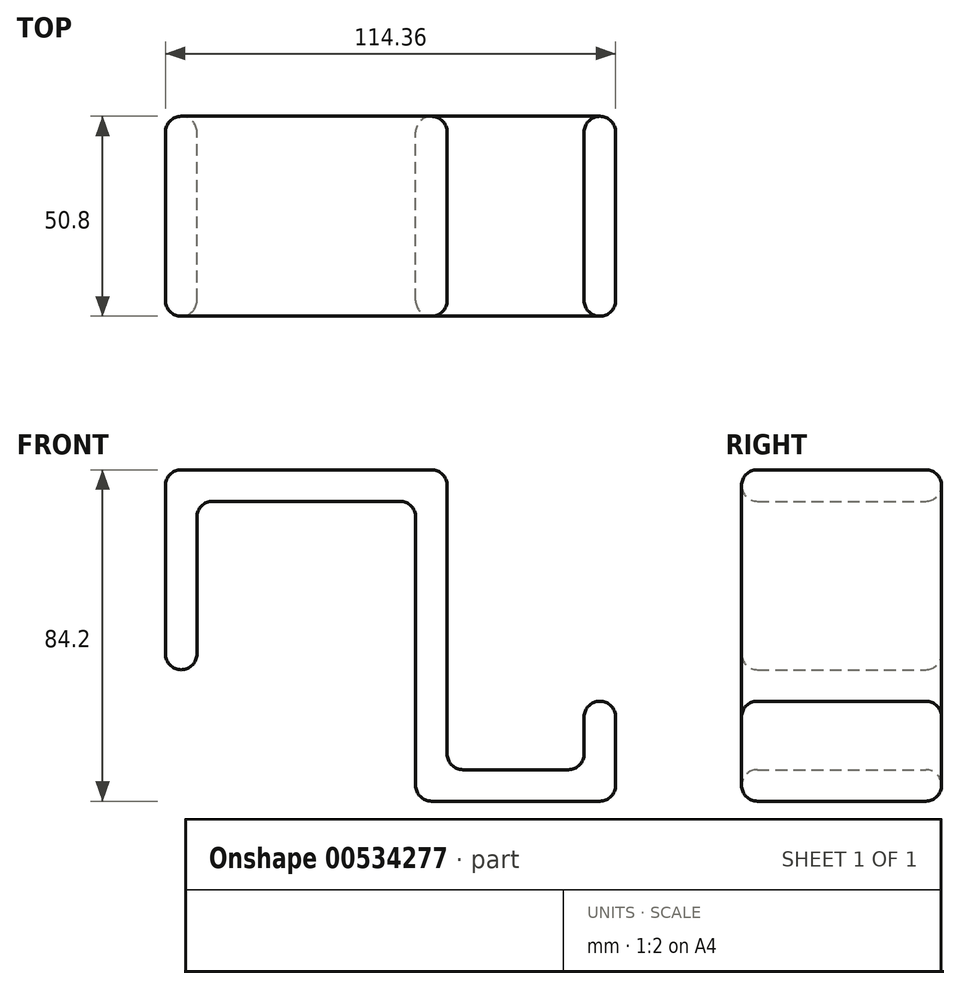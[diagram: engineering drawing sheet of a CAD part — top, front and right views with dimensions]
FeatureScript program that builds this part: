
annotation { "Feature Type Name" : "Feature", "Feature Type Description" : "" }
export const myFeature = defineFeature(function(context is Context, id is Id, definition is map)
    precondition{}
    {
        {
            var Q0;
            Q0=qCreatedBy(makeId("Front.planeOp"),FACE);
            var sketch = newSketch(context, id + "F0", { "sketchPlane" : qUnion([Q0])});
            skLineSegment(sketch, "E0", {"start": v(0, 0) * mm, "end": v(71.56, 0) * mm});
            skLineSegment(sketch, "E1", {"start": v(71.56, 0) * mm, "end": v(71.56, -76.2) * mm});
            skLineSegment(sketch, "E2", {"start": v(63.56, -84.2) * mm, "end": v(63.56, -8) * mm});
            skLineSegment(sketch, "E3", {"start": v(63.56, -8) * mm, "end": v(8, -8) * mm});
            skLineSegment(sketch, "E4", {"start": v(8, -8) * mm, "end": v(8, -50.8) * mm});
            skLineSegment(sketch, "E5", {"start": v(8, -50.8) * mm, "end": v(0, -50.8) * mm});
            skLineSegment(sketch, "E6", {"start": v(0, -50.8) * mm, "end": v(0, 0) * mm});
            skLineSegment(sketch, "E7", {"start": v(71.56, -76.2) * mm, "end": v(106.36, -76.2) * mm});
            skLineSegment(sketch, "E8", {"start": v(106.36, -76.2) * mm, "end": v(106.36, -58.8) * mm});
            skLineSegment(sketch, "E9", {"start": v(106.36, -58.8) * mm, "end": v(114.36, -58.8) * mm});
            skLineSegment(sketch, "E10", {"start": v(114.36, -58.8) * mm, "end": v(114.36, -84.2) * mm});
            skLineSegment(sketch, "E11", {"start": v(114.36, -84.2) * mm, "end": v(63.56, -84.2) * mm});
            skSolve(sketch);
        }
        {
            var Q0;
            Q0 = qSketchRegion(id + "F0", true);
            extrude(context, id + "F1", {"entities" : qUnion([Q0]), "depth" : 50.8 * mm, "offsetDistance" : 25 * mm});
        }
        {
            var Q0;
            Q0=makeQuery(id+"F1.opExtrude","SWEPT_EDGE",EDGE,{"disambiguationData":[OSD([sQuery(id+"F0.wireOp",EDGE,"E0"),sQuery(id+"F0.wireOp",EDGE,"E6")])]});
            var Q1;
            Q1=makeQuery(id+"F1.opExtrude","SWEPT_EDGE",EDGE,{"disambiguationData":[OSD([sQuery(id+"F0.wireOp",EDGE,"E0"),sQuery(id+"F0.wireOp",EDGE,"E1")])]});
            var Q2;
            Q2=makeQuery(id+"F1.opExtrude","SWEPT_EDGE",EDGE,{"disambiguationData":[OSD([sQuery(id+"F0.wireOp",EDGE,"E1"),sQuery(id+"F0.wireOp",EDGE,"E7")])]});
            var Q3;
            Q3=makeQuery(id+"F1.opExtrude","SWEPT_EDGE",EDGE,{"disambiguationData":[OSD([sQuery(id+"F0.wireOp",EDGE,"E7"),sQuery(id+"F0.wireOp",EDGE,"E8")])]});
            var Q4;
            Q4=makeQuery(id+"F1.opExtrude","CAP_EDGE",EDGE,{"disambiguationData":[OSD([sQuery(id+"F0.wireOp",EDGE,"E1")])],"isStart":false});
            var Q5;
            Q5=makeQuery(id+"F1.opExtrude","CAP_EDGE",EDGE,{"disambiguationData":[OSD([sQuery(id+"F0.wireOp",EDGE,"E1")])],"isStart":true});
            var Q6;
            Q6=makeQuery(id+"F1.opExtrude","CAP_EDGE",EDGE,{"disambiguationData":[OSD([sQuery(id+"F0.wireOp",EDGE,"E9")])],"isStart":true});
            var Q7;
            Q7=makeQuery(id+"F1.opExtrude","SWEPT_EDGE",EDGE,{"disambiguationData":[OSD([sQuery(id+"F0.wireOp",EDGE,"E9"),sQuery(id+"F0.wireOp",EDGE,"E10")])]});
            var Q8;
            Q8=makeQuery(id+"F1.opExtrude","CAP_EDGE",EDGE,{"disambiguationData":[OSD([sQuery(id+"F0.wireOp",EDGE,"E9")])],"isStart":false});
            var Q9;
            Q9=makeQuery(id+"F1.opExtrude","SWEPT_EDGE",EDGE,{"disambiguationData":[OSD([sQuery(id+"F0.wireOp",EDGE,"E8"),sQuery(id+"F0.wireOp",EDGE,"E9")])]});
            var Q10;
            Q10=makeQuery(id+"F1.opExtrude","SWEPT_EDGE",EDGE,{"disambiguationData":[OSD([sQuery(id+"F0.wireOp",EDGE,"E10"),sQuery(id+"F0.wireOp",EDGE,"E11")])]});
            var Q11;
            Q11=makeQuery(id+"F1.opExtrude","CAP_EDGE",EDGE,{"disambiguationData":[OSD([sQuery(id+"F0.wireOp",EDGE,"E10")])],"isStart":false});
            var Q12;
            Q12=makeQuery(id+"F1.opExtrude","CAP_EDGE",EDGE,{"disambiguationData":[OSD([sQuery(id+"F0.wireOp",EDGE,"E10")])],"isStart":true});
            var Q13;
            Q13=makeQuery(id+"F1.opExtrude","CAP_EDGE",EDGE,{"disambiguationData":[OSD([sQuery(id+"F0.wireOp",EDGE,"E11")])],"isStart":true});
            var Q14;
            Q14=makeQuery(id+"F1.opExtrude","CAP_EDGE",EDGE,{"disambiguationData":[OSD([sQuery(id+"F0.wireOp",EDGE,"E11")])],"isStart":false});
            var Q15;
            Q15=makeQuery(id+"F1.opExtrude","SWEPT_EDGE",EDGE,{"disambiguationData":[OSD([sQuery(id+"F0.wireOp",EDGE,"E2"),sQuery(id+"F0.wireOp",EDGE,"E11")])]});
            var Q16;
            Q16=makeQuery(id+"F1.opExtrude","CAP_EDGE",EDGE,{"disambiguationData":[OSD([sQuery(id+"F0.wireOp",EDGE,"E2")])],"isStart":false});
            var Q17;
            Q17=makeQuery(id+"F1.opExtrude","CAP_EDGE",EDGE,{"disambiguationData":[OSD([sQuery(id+"F0.wireOp",EDGE,"E2")])],"isStart":true});
            var Q18;
            Q18=makeQuery(id+"F1.opExtrude","CAP_EDGE",EDGE,{"disambiguationData":[OSD([sQuery(id+"F0.wireOp",EDGE,"E6")])],"isStart":true});
            var Q19;
            Q19=makeQuery(id+"F1.opExtrude","CAP_EDGE",EDGE,{"disambiguationData":[OSD([sQuery(id+"F0.wireOp",EDGE,"E6")])],"isStart":false});
            var Q20;
            Q20=makeQuery(id+"F1.opExtrude","SWEPT_EDGE",EDGE,{"disambiguationData":[OSD([sQuery(id+"F0.wireOp",EDGE,"E5"),sQuery(id+"F0.wireOp",EDGE,"E6")])]});
            var Q21;
            Q21=makeQuery(id+"F1.opExtrude","CAP_EDGE",EDGE,{"disambiguationData":[OSD([sQuery(id+"F0.wireOp",EDGE,"E7")])],"isStart":true});
            var Q22;
            Q22=makeQuery(id+"F1.opExtrude","CAP_EDGE",EDGE,{"disambiguationData":[OSD([sQuery(id+"F0.wireOp",EDGE,"E4")])],"isStart":true});
            var Q23;
            Q23=makeQuery(id+"F1.opExtrude","CAP_EDGE",EDGE,{"disambiguationData":[OSD([sQuery(id+"F0.wireOp",EDGE,"E4")])],"isStart":false});
            var Q24;
            Q24=makeQuery(id+"F1.opExtrude","CAP_EDGE",EDGE,{"disambiguationData":[OSD([sQuery(id+"F0.wireOp",EDGE,"E3")])],"isStart":false});
            var Q25;
            Q25=makeQuery(id+"F1.opExtrude","CAP_EDGE",EDGE,{"disambiguationData":[OSD([sQuery(id+"F0.wireOp",EDGE,"E7")])],"isStart":false});
            var Q26;
            Q26=makeQuery(id+"F1.opExtrude","CAP_EDGE",EDGE,{"disambiguationData":[OSD([sQuery(id+"F0.wireOp",EDGE,"E8")])],"isStart":true});
            var Q27;
            Q27=makeQuery(id+"F1.opExtrude","CAP_EDGE",EDGE,{"disambiguationData":[OSD([sQuery(id+"F0.wireOp",EDGE,"E5")])],"isStart":false});
            var Q28;
            Q28=makeQuery(id+"F1.opExtrude","CAP_EDGE",EDGE,{"disambiguationData":[OSD([sQuery(id+"F0.wireOp",EDGE,"E8")])],"isStart":false});
            var Q29;
            Q29=makeQuery(id+"F1.opExtrude","SWEPT_EDGE",EDGE,{"disambiguationData":[OSD([sQuery(id+"F0.wireOp",EDGE,"E4"),sQuery(id+"F0.wireOp",EDGE,"E5")])]});
            var Q30;
            Q30=makeQuery(id+"F1.opExtrude","CAP_EDGE",EDGE,{"disambiguationData":[OSD([sQuery(id+"F0.wireOp",EDGE,"E0")])],"isStart":false});
            var Q31;
            Q31=makeQuery(id+"F1.opExtrude","CAP_EDGE",EDGE,{"disambiguationData":[OSD([sQuery(id+"F0.wireOp",EDGE,"E0")])],"isStart":true});
            var Q32;
            Q32=makeQuery(id+"F1.opExtrude","SWEPT_EDGE",EDGE,{"disambiguationData":[OSD([sQuery(id+"F0.wireOp",EDGE,"E3"),sQuery(id+"F0.wireOp",EDGE,"E4")])]});
            var Q33;
            Q33=makeQuery(id+"F1.opExtrude","SWEPT_EDGE",EDGE,{"disambiguationData":[OSD([sQuery(id+"F0.wireOp",EDGE,"E2"),sQuery(id+"F0.wireOp",EDGE,"E3")])]});
            var Q34;
            Q34=makeQuery(id+"F1.opExtrude","CAP_EDGE",EDGE,{"disambiguationData":[OSD([sQuery(id+"F0.wireOp",EDGE,"E5")])],"isStart":true});
            var Q35;
            Q35=makeQuery(id+"F1.opExtrude","CAP_EDGE",EDGE,{"disambiguationData":[OSD([sQuery(id+"F0.wireOp",EDGE,"E3")])],"isStart":true});
            fillet(context, id + "F2", {"entities" : qUnion([Q0, Q1, Q2, Q3, Q4, Q5, Q6, Q7, Q8, Q9, Q10, Q11, Q12, Q13, Q14, Q15, Q16, Q17, Q18, Q19, Q20, Q21, Q22, Q23, Q24, Q25, Q26, Q27, Q28, Q29, Q30, Q31, Q32, Q33, Q34, Q35]), "radius" : 4 * mm, "tangentPropagation" : true, "allowEdgeOverflow" : false});
        }
    });
